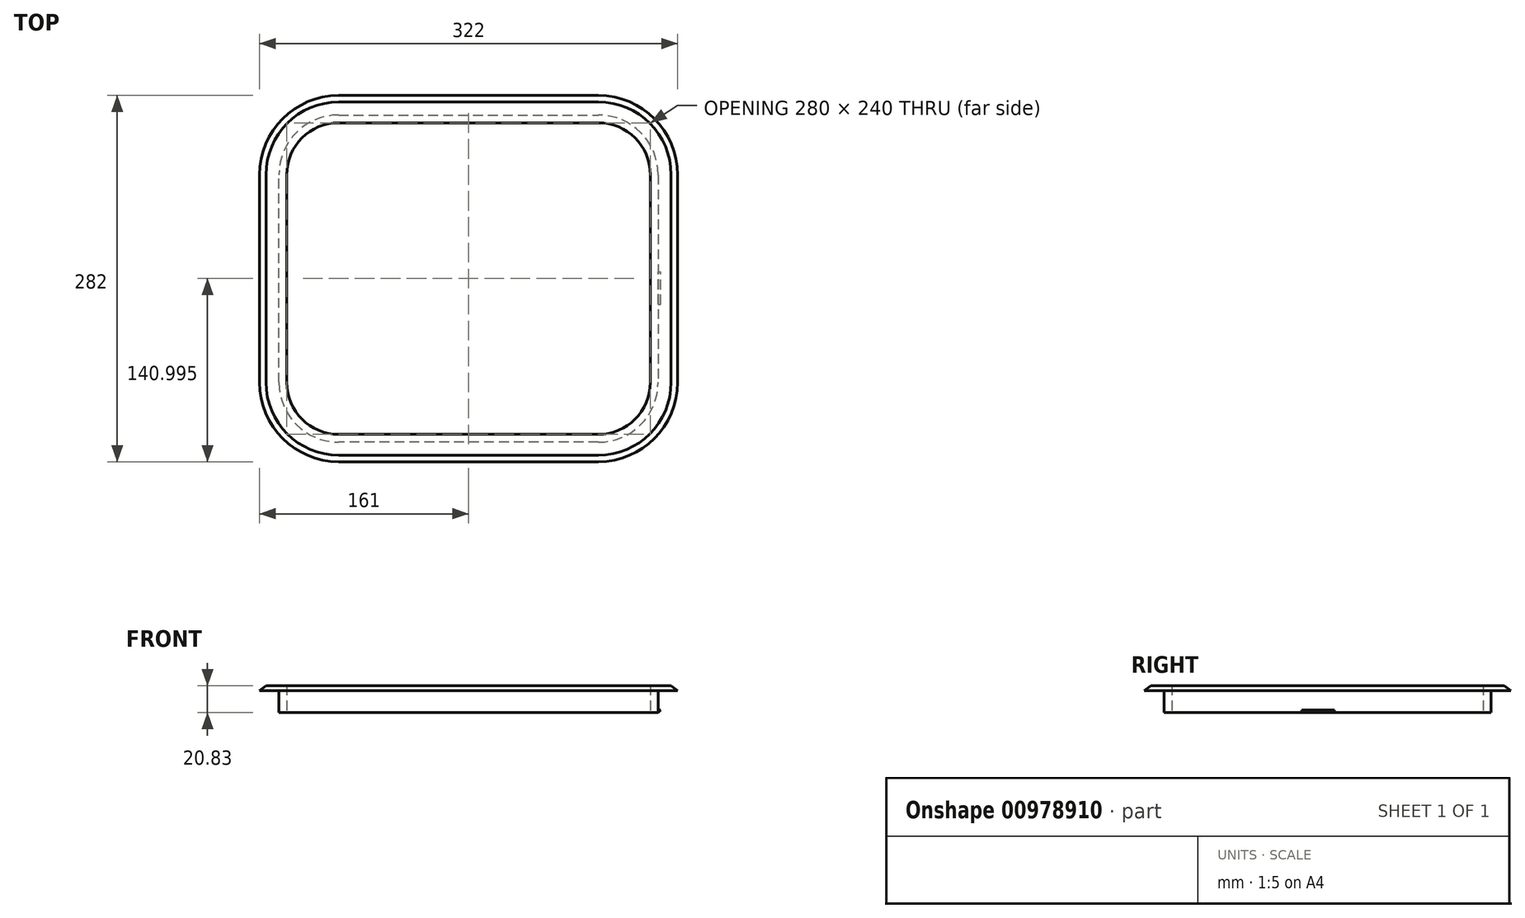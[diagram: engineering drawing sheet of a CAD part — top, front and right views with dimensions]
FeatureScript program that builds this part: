
annotation { "Feature Type Name" : "Feature", "Feature Type Description" : "" }
export const myFeature = defineFeature(function(context is Context, id is Id, definition is map)
    precondition{}
    {
        {
            var Q0;
            Q0=qCreatedBy(makeId("Front.planeOp"),FACE);
            var sketch = newSketch(context, id + "F0", { "sketchPlane" : qUnion([Q0])});
            skLineSegment(sketch, "E0.bottom", {"start": v(0, 0) * mm, "end": v(16, 0) * mm});
            skLineSegment(sketch, "E0.top", {"start": v(0, 4) * mm, "end": v(16, 4) * mm});
            skLineSegment(sketch, "E0.left", {"start": v(0, 0) * mm, "end": v(0, 4) * mm});
            skLineSegment(sketch, "E0.right", {"start": v(16, 0) * mm, "end": v(16, 4) * mm});
            skLineSegment(sketch, "E1", {"start": v(16, 4) * mm, "end": v(21, 0) * mm});
            skLineSegment(sketch, "E2", {"start": v(21, 0) * mm, "end": v(16, 0) * mm});
            skLineSegment(sketch, "E3.bottom", {"start": v(0, 0) * mm, "end": v(6, 0) * mm});
            skLineSegment(sketch, "E3.top", {"start": v(0, -16.83) * mm, "end": v(6, -16.83) * mm});
            skLineSegment(sketch, "E3.left", {"start": v(0, 0) * mm, "end": v(0, -16.83) * mm});
            skLineSegment(sketch, "E3.right", {"start": v(6, 0) * mm, "end": v(6, -16.83) * mm});
            skSolve(sketch);
        }
        {
            var Q0;
            Q0=qCreatedBy(makeId("Top.planeOp"),FACE);
            var sketch = newSketch(context, id + "F1", { "sketchPlane" : qUnion([Q0])});
            skLineSegment(sketch, "E4.top", {"start": v(-40, 114.77) * mm, "end": v(-240, 114.77) * mm});
            skLineSegment(sketch, "E4.right", {"start": v(-280, -85.23) * mm, "end": v(-280, 74.77) * mm});
            skPoint(sketch, "E5.visualSharp", {"position": v(0, 114.77) * mm});
            skArc(sketch, "E5.filletArc", {"start": v(0, 74.77) * mm, "mid": v(-11.72, 103.05) * mm, "end": v(-40, 114.77) * mm});
            skPoint(sketch, "E6.visualSharp", {"position": v(-280, 114.77) * mm});
            skArc(sketch, "E6.filletArc", {"start": v(-240, 114.77) * mm, "mid": v(-268.28, 103.05) * mm, "end": v(-280, 74.77) * mm});
            skPoint(sketch, "E7.visualSharp", {"position": v(-280, -79.77) * mm});
            skArc(sketch, "E7.filletArc", {"start": v(-280, -85.23) * mm, "mid": v(-268.28, -113.52) * mm, "end": v(-240, -125.23) * mm});
            skPoint(sketch, "E8", {"position": v(0, -125.23) * mm});
            skLineSegment(sketch, "E9", {"start": v(-240, -125.23) * mm, "end": v(-40, -125.23) * mm});
            skLineSegment(sketch, "E10", {"start": v(0, 74.77) * mm, "end": v(0, -85.23) * mm});
            skArc(sketch, "E11.filletArc", {"start": v(-40, -125.23) * mm, "mid": v(-11.72, -113.52) * mm, "end": v(0, -85.23) * mm});
            skSolve(sketch);
        }
        {
            var Q0;
            Q0 = qSketchRegion(id + "F0", true);
            var Q1;
            Q1 = qConstructionFilter(qBodyType(qCreatedBy(id + "F1" ,EDGE), BodyType.WIRE), ConstructionObject.NO);
            sweep(context, id + "F2", {"profiles" : qUnion([Q0]), "path" : qUnion([Q1])});
        }
        {
            var Q0;
            Q0=qCreatedBy(makeId("Front.planeOp"),FACE);
            var sketch = newSketch(context, id + "F3", { "sketchPlane" : qUnion([Q0])});
            skLineSegment(sketch, "E12.top", {"start": v(6.02, -14.76) * mm, "end": v(8.04, -14.76) * mm});
            skLineSegment(sketch, "E12.left", {"start": v(6.02, -16.8) * mm, "end": v(6.02, -14.76) * mm});
            skLineSegment(sketch, "E13", {"start": v(8.04, -14.76) * mm, "end": v(6.02, -16.8) * mm});
            skSolve(sketch);
        }
        {
            var Q0;
            Q0 = qSketchRegion(id + "F3", true);
            extrude(context, id + "F4", {"entities" : qUnion([Q0]), "depth" : 25 * mm, "offsetDistance" : 25 * mm});
        }
    });
